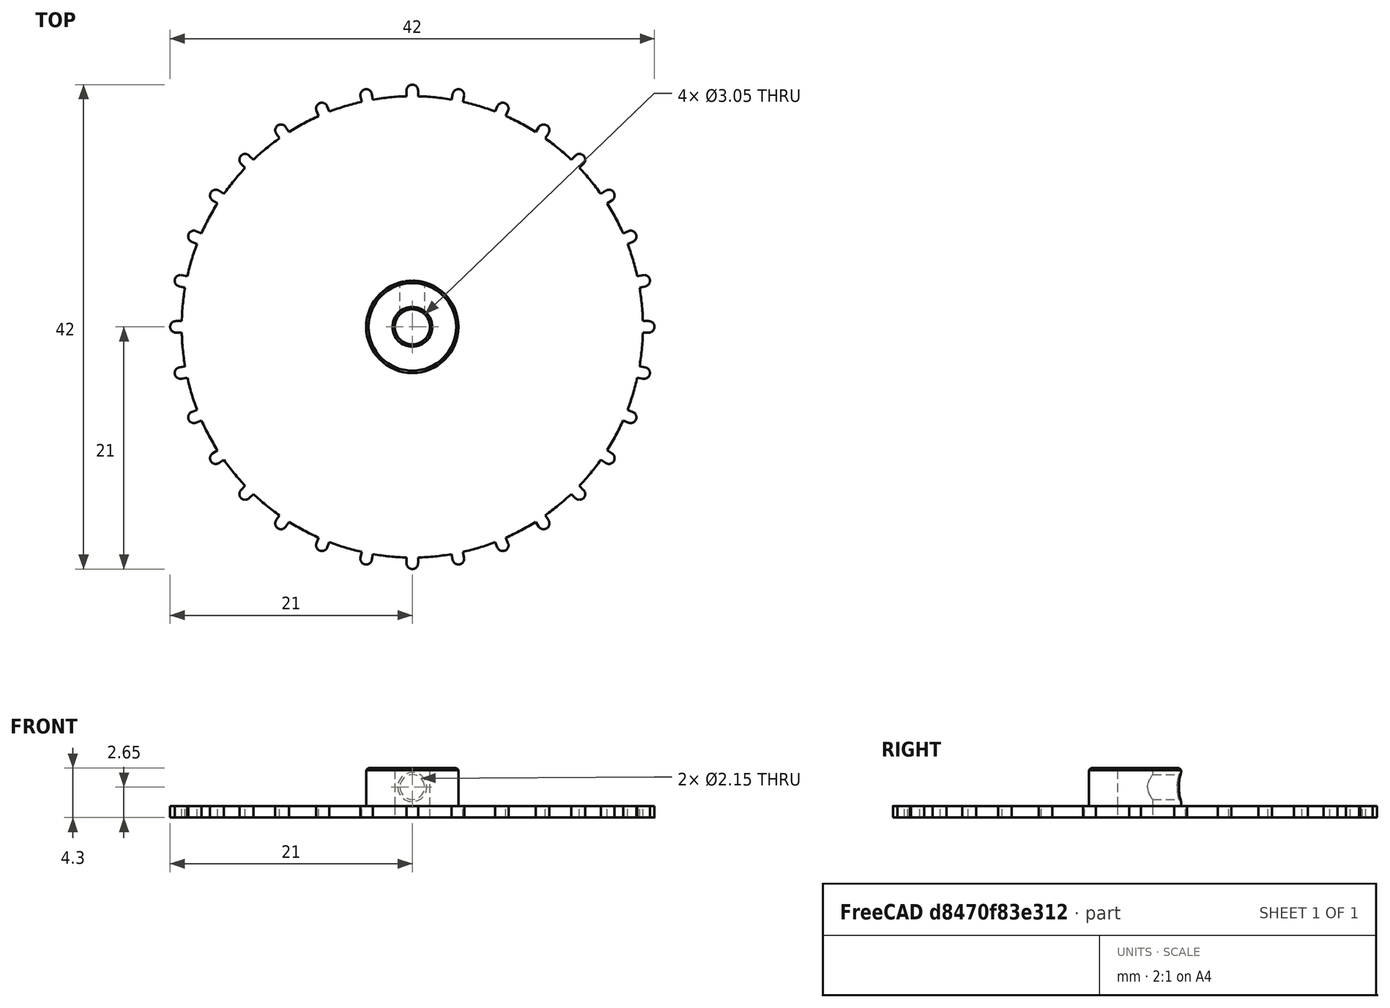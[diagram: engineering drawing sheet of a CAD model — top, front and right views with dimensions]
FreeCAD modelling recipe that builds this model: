
FCSTD DOCUMENT  (FreeCAD 0.20R29603 (Git))
Label: gear-with-hub
License: Other
objects: TechDraw::DrawViewDimension×7, Sketcher::SketchObject×4, PartDesign::Body×3, PartDesign::Pad×2, PartDesign::Chamfer×2, TechDraw::DrawViewPart×2, TechDraw::DrawViewBalloon×2, PartDesign::Hole×1, PartDesign::PolarPattern×1, PartDesign::Pocket×1, PartDesign::Boolean×1, TechDraw::DrawSVGTemplate×1, TechDraw::DrawLeaderLine×1, TechDraw::DrawViewAnnotation×1, TechDraw::DrawPage×1
note: 21 computed .brp shape members not serialized (recipe doc carries the construction recipe); baked Part::Feature solids carry a one-line shape summary decoded from their .brp

FEATURE [Sketcher::SketchObject] Sketch
  FullyConstrained = true
  MapMode = 5
  Support = -> [XY_Plane]
  sketch-geometry (3):
    g0: Circle CenterX=0 CenterY=0 CenterZ=0 NormalX=0 NormalY=0 NormalZ=1 AngleXU=0 Radius=4
    g1: Circle CenterX=0 CenterY=0 CenterZ=0 NormalX=0 NormalY=0 NormalZ=1 AngleXU=0 Radius=1.525
    g2: LineSegment StartX=1.525 StartY=0 StartZ=0 EndX=4 EndY=0 EndZ=0
  constraints (9):
    c: Coincident(g1,g0)
    c: Coincident(g0,g-1)
    c: Diameter(g1) = 3.05
    c: Diameter(g0) = 8
    c: PointOnObject(g2,g1)
    c: PointOnObject(g2,g0)
    c: Horizontal(g2)
    c: PointOnObject(g2,g-1)
    c: DistanceX(g2,g2) = 2.475
FEATURE [PartDesign::Pad] Pad
  Direction = (0,0,1)
  Length = 3.3
  Length2 = 10
  Profile = -> Sketch
  ReferenceAxis = -> Sketch [N_Axis]
  Type = 0
FEATURE [Sketcher::SketchObject] Sketch001
  FullyConstrained = false
  MapMode = 5
  Placement = pos=(0,0,0) rot=(1,0,0;1.5708rad)
  Support = -> [XZ_Plane]
  sketch-geometry (2):
    g0: GeomPoint X=0 Y=1.65 Z=0
    g1: Circle CenterX=0 CenterY=1.65 CenterZ=0 NormalX=0 NormalY=0 NormalZ=1 AngleXU=0 Radius=2.07621
  constraints (3):
    c: PointOnObject(g0,g-2)
    c: Coincident(g1,g0)
    c: DistanceY(g-1,g1) = 1.65
FEATURE [PartDesign::Hole] Hole  label="M2.5x0.45 Hole"
  BaseFeature = -> Pad
  CustomThreadClearance = 0
  Depth = 5
  DepthType = 0
  Diameter = 2.15
  DrillForDepth = false
  DrillPoint = 1
  DrillPointAngle = 118
  HoleCutCountersinkAngle = 90
  HoleCutCustomValues = false
  HoleCutDepth = 0
  HoleCutDiameter = 6.1
  HoleCutType = 0
  ModelThread = false
  Profile = -> Sketch001
  Tapered = false
  TaperedAngle = 90
  ThreadClass = 0
  ThreadDepth = 5
  ThreadDepthType = 0
  ThreadDirection = 0
  ThreadFit = 0
  ThreadSize = 8
  ThreadType = 2
  Threaded = true
  UseCustomThreadClearance = false
FEATURE [PartDesign::Chamfer] Chamfer
  Angle = 45
  Base = -> Hole [Edge4]
  BaseFeature = -> Hole
  ChamferType = 0
  FlipDirection = false
  Size = 0.2
  Size2 = 1
  SupportTransform = false
  UseAllEdges = false
FEATURE [Sketcher::SketchObject] Sketch002
  FullyConstrained = true
  MapMode = 5
  Support = -> [XY_Plane001]
  sketch-geometry (7):
    g0: LineSegment StartX=-0.5 StartY=19.9937 StartZ=0 EndX=-0.5 EndY=20.5 EndZ=0
    g1: ArcOfCircle CenterX=0 CenterY=20.5 CenterZ=0 NormalX=0 NormalY=0 NormalZ=1 AngleXU=0 Radius=0.5 StartAngle=6.28319 EndAngle=9.42478
    g2: LineSegment StartX=0.5 StartY=20.5 StartZ=0 EndX=0.5 EndY=19.9937 EndZ=0
    g3: ArcOfCircle CenterX=0 CenterY=0 CenterZ=0 NormalX=0 NormalY=0 NormalZ=1 AngleXU=0 Radius=20 StartAngle=1.39945 EndAngle=1.54579
    g4: ArcOfCircle CenterX=0 CenterY=0 CenterZ=0 NormalX=0 NormalY=0 NormalZ=1 AngleXU=0 Radius=20 StartAngle=1.54579 EndAngle=1.5958
    g5: LineSegment StartX=-0.5 StartY=19.9937 StartZ=0 EndX=1e-16 EndY=0 EndZ=0
    g6: LineSegment StartX=3.41019 StartY=19.7071 StartZ=0 EndX=0 EndY=0 EndZ=0
  constraints (20):
    c: Coincident(g2,g1)
    c: Vertical(g2)
    c: Coincident(g3,g2)
    c: Diameter(g3) = 40
    c: DistanceY(g3,g1) = 20.5
    c: Coincident(g4,g3)
    c: Coincident(g4,g0)
    c: Coincident(g4,g2)
    c: Tangent(g2,g1)
    c: Coincident(g6,g3)
    c: Coincident(g6,g3)
    c: Angle(g6,g5) = 0.19635
    c: Coincident(g5,g0)
    c: Coincident(g0,g1)
    c: Tangent(g0,g1)
    c: Vertical(g0)
    c: Coincident(g5,g3)
    c: Coincident(g3,g-1)
    c: PointOnObject(g1,g-2)
    c: Diameter(g1) = 1
FEATURE [PartDesign::Pad] Pad001
  Direction = (0,0,1)
  Length = 1
  Length2 = 100
  Profile = -> Sketch002
  Type = 0
FEATURE [Sketcher::SketchObject] Sketch003
  FullyConstrained = true
  MapMode = 5
  Support = -> [XY_Plane001]
  sketch-geometry (22):
    g0: Circle CenterX=0 CenterY=-11 CenterZ=0 NormalX=0 NormalY=0 NormalZ=1 AngleXU=0 Radius=1.5
    g1: Circle CenterX=9.52628 CenterY=5.5 CenterZ=0 NormalX=0 NormalY=0 NormalZ=1 AngleXU=0 Radius=1.5
    g2: Circle CenterX=-9.52628 CenterY=5.5 CenterZ=0 NormalX=0 NormalY=0 NormalZ=1 AngleXU=0 Radius=1.5
    g3: ArcOfCircle CenterX=0 CenterY=10 CenterZ=0 NormalX=0 NormalY=0 NormalZ=1 AngleXU=0 Radius=1.5 StartAngle=3.14159 EndAngle=6.28319
    g4: ArcOfCircle CenterX=-1e-16 CenterY=12 CenterZ=0 NormalX=0 NormalY=0 NormalZ=1 AngleXU=0 Radius=1.5 StartAngle=1e-16 EndAngle=3.14159
    g5: LineSegment StartX=1.5 StartY=10 StartZ=0 EndX=1.5 EndY=12 EndZ=0
    g6: LineSegment StartX=-1.5 StartY=10 StartZ=0 EndX=-1.5 EndY=12 EndZ=0
    g7: ArcOfCircle CenterX=8.66025 CenterY=-5 CenterZ=0 NormalX=0 NormalY=0 NormalZ=1 AngleXU=0 Radius=1.5 StartAngle=1.0472 EndAngle=4.18879
    g8: ArcOfCircle CenterX=10.3923 CenterY=-6 CenterZ=0 NormalX=0 NormalY=0 NormalZ=1 AngleXU=0 Radius=1.5 StartAngle=4.18879 EndAngle=7.33038
    g9: LineSegment StartX=7.91025 StartY=-6.29904 StartZ=0 EndX=9.6423 EndY=-7.29904 EndZ=0
    g10: LineSegment StartX=9.41025 StartY=-3.70096 StartZ=0 EndX=11.1423 EndY=-4.70096 EndZ=0
    g11: ArcOfCircle CenterX=-8.66025 CenterY=-5 CenterZ=0 NormalX=0 NormalY=0 NormalZ=1 AngleXU=0 Radius=1.5 StartAngle=5.23599 EndAngle=8.37758
    g12: ArcOfCircle CenterX=-10.3923 CenterY=-6 CenterZ=0 NormalX=0 NormalY=0 NormalZ=1 AngleXU=0 Radius=1.5 StartAngle=2.0944 EndAngle=5.23599
    g13: LineSegment StartX=-9.41025 StartY=-3.70096 StartZ=0 EndX=-11.1423 EndY=-4.70096 EndZ=0
    g14: LineSegment StartX=-7.91025 StartY=-6.29904 StartZ=0 EndX=-9.6423 EndY=-7.29904 EndZ=0
    g15: LineSegment StartX=-10.3923 StartY=-6 StartZ=0 EndX=-8.66025 EndY=-5 EndZ=0
    g16: LineSegment StartX=8.66025 StartY=-5 StartZ=0 EndX=10.3923 EndY=-6 EndZ=0
    g17: LineSegment StartX=-9.52628 StartY=5.5 StartZ=0 EndX=0 EndY=0 EndZ=0
    g18: LineSegment StartX=9.52628 StartY=5.5 StartZ=0 EndX=0 EndY=0 EndZ=0
    g19: Circle CenterX=0 CenterY=0 CenterZ=0 NormalX=0 NormalY=0 NormalZ=1 AngleXU=0 Radius=1.525
    g20: Circle CenterX=0 CenterY=-4.2625 CenterZ=0 NormalX=0 NormalY=0 NormalZ=1 AngleXU=0 Radius=1.3
    g21: Circle CenterX=0 CenterY=4.2625 CenterZ=0 NormalX=0 NormalY=0 NormalZ=1 AngleXU=0 Radius=1.3
  constraints (55):
    c: PointOnObject(g0,g-2)
    c: Tangent(g3,g6) = 1.5708
    c: Tangent(g3,g5) = -1.5708
    c: Tangent(g5,g4) = -1.5708
    c: Tangent(g6,g4) = 1.5708
    c: Vertical(g5)
    c: Equal(g3,g4)
    c: PointOnObject(g3,g-2)
    c: Tangent(g7,g10) = 1.5708
    c: Tangent(g7,g9) = -1.5708
    c: Tangent(g9,g8) = -1.5708
    c: Tangent(g10,g8) = 1.5708
    c: Equal(g7,g8)
    c: Tangent(g11,g14) = 1.5708
    c: Tangent(g11,g13) = -1.5708
    c: Tangent(g13,g12) = -1.5708
    c: Tangent(g14,g12) = 1.5708
    c: Equal(g11,g12)
    c: Coincident(g15,g12)
    c: Coincident(g15,g11)
    c: Coincident(g16,g7)
    c: Coincident(g16,g8)
    c: Angle(g-1,g16) = 2.61799
    c: Angle(g-1,g15) = 0.523599
    c: Diameter(g11) = 3
    c: Diameter(g7) = 3
    c: Diameter(g3) = 3
    c: PointOnObject(g-1,g15)
    c: PointOnObject(g-1,g16)
    c: Coincident(g17,g2)
    c: Coincident(g17,g-1)
    c: Coincident(g18,g1)
    c: Coincident(g18,g-1)
    c: Angle(g18,g-2) = 1.0472
    c: Angle(g-2,g17) = 1.0472
    c: Distance(g11,g-1) = 10
    c: Distance(g-1,g12) = 12
    c: Distance(g18) = 11
    c: Distance(g17) = 11
    c: Distance(g-1,g0) = 11
    c: Distance(g7,g-1) = 10
    c: Distance(g8,g-1) = 12
    c: Distance(g3,g-1) = 10
    c: Distance(g-1,g4) = 12
    c: Diameter(g1) = 3
    c: Diameter(g2) = 3
    c: Diameter(g0) = 3
    c: Coincident(g19,g-1)
    c: Diameter(g19) = 3.05
    c: PointOnObject(g20,g-2)
    c: Equal(g21,g20)
    c: Symmetric(g21,g20,g-1)
    c: DistanceY(g20,g21) = 8.525
    c: Diameter(g20) = 2.6
    c: Diameter(g19) = 3.05
FEATURE [PartDesign::PolarPattern] PolarPattern
  Angle = 360
  Axis = -> Sketch002 [N_Axis]
  BaseFeature = -> Pad001
  Occurrences = 32
  Originals = -> [Pad001]
FEATURE [PartDesign::Pocket] Pocket
  BaseFeature = -> PolarPattern
  Direction = (0,0,-1)
  Length = 5
  Length2 = 100
  Profile = -> Sketch003
  Reversed = true
  Type = 0
FEATURE [PartDesign::Body] Body001
  Group = -> [Sketch002,Pad001,PolarPattern,Sketch003,Pocket]
  Origin = -> Origin001
  Placement = pos=(0,0,-1) rot=(0,0,1;0rad)
  Tip = -> Pocket
FEATURE [PartDesign::Chamfer] Chamfer001
  Angle = 45
  Base = -> Chamfer [Edge4,Edge8]
  BaseFeature = -> Chamfer
  ChamferType = 0
  FlipDirection = false
  Size = 0.2
  Size2 = 1
  SupportTransform = false
  UseAllEdges = false
FEATURE [PartDesign::Body] Body
  Group = -> [Sketch,Pad,Sketch001,Hole,Chamfer,Chamfer001]
  Origin = -> Origin
  Tip = -> Chamfer001
FEATURE [PartDesign::Boolean] Boolean
  Group = -> [Body001,Body]
  Type = 0
FEATURE [PartDesign::Body] Body002
  Group = -> [Boolean]
  Origin = -> Origin002
  Tip = -> Boolean
FEATURE [TechDraw::DrawSVGTemplate] Template
  EditableTexts = Designed_by_Name=Lucian Chapar; Drawing_number=PENDING; FC-Date=2023-02-15; FC-SC=4:1; FC-SH=1 OF 1; FC-Title=1-piece-gear; Weight=N/A
  Height = 210
  Orientation = 1
  Width = 297
FEATURE [TechDraw::DrawViewPart] View001
  CoarseView = false
  Direction = (-0.366,0.715,0.596)
  Focus = 100
  HardHidden = false
  IsoCount = 0
  IsoHidden = false
  IsoVisible = false
  LockPosition = false
  Perspective = false
  Rotation = 0
  Scale = 4
  ScaleType = 0
  SeamHidden = false
  SeamVisible = false
  SmoothHidden = false
  SmoothVisible = false
  Source = -> [Body002]
  X = 152.816
  XDirection = (-0.887,-0.461,0.009)
  Y = 146.518
FEATURE [TechDraw::DrawViewBalloon] Balloon
  BubbleShape = 1
  EndType = 0
  EndTypeScale = 1
  KinkLength = 21
  LockPosition = false
  OriginX = -2.04745
  OriginY = -0.847764
  Rotation = 0
  Scale = 4
  ScaleType = 0
  ShapeScale = 1
  SourceView = -> View001
  Text = M2.5x0.45 ↧ 7
  TextWrapLen = -1
  X = -24.7749
  Y = -8.90589
FEATURE [TechDraw::DrawLeaderLine] LeaderLine
  AutoHorizontal = true
  EndSymbol = 0
  LeaderParent = -> View001
  LockPosition = true
  Rotation = 0
  Scalable = false
  Scale = 4
  ScaleType = 0
  StartSymbol = 0
  WayPoints = (3) [(0,0,0),(871.108,-115.163,0),(32.482,-115.163,0)]
  X = 1.18375
  Y = 2.07652
FEATURE [TechDraw::DrawViewAnnotation] Annotation001
  Font = osifont
  LineSpace = 80
  LockPosition = false
  MaxWidth = -1
  Rotation = 0
  Scale = 4
  ScaleType = 0
  Text = ⌵0.2x45°
  TextSize = 6
  TextStyle = 0
  X = 257.591
  Y = 163.629
FEATURE [TechDraw::DrawViewDimension] Dimension
  AngleOverride = false
  Arbitrary = true
  ArbitraryTolerances = false
  EqualTolerance = false
  ExtensionAngle = 0
  FormatSpec = ⌀3.05
  FormatSpecOverTolerance = %+.2w
  FormatSpecUnderTolerance = %+.2w
  Inverted = false
  LineAngle = 0
  LockPosition = false
  MeasureType = 1
  OverTolerance = 0
  References2D = -> [View001]
  Rotation = 0
  Scale = 4
  ScaleType = 0
  TheoreticalExact = false
  Type = 5
  UnderTolerance = -0.02
  X = -118.545
  Y = 6.44192
FEATURE [TechDraw::DrawViewDimension] Dimension001
  AngleOverride = false
  Arbitrary = true
  ArbitraryTolerances = false
  EqualTolerance = false
  ExtensionAngle = 0
  FormatSpec = R20
  FormatSpecOverTolerance = %+.2w
  FormatSpecUnderTolerance = %+.2w
  Inverted = false
  LineAngle = 0
  LockPosition = false
  MeasureType = 1
  OverTolerance = 0
  References2D = -> [View001]
  Rotation = 0
  Scale = 4
  ScaleType = 0
  TheoreticalExact = true
  Type = 4
  UnderTolerance = 0
  X = 91.1366
  Y = -42.2632
FEATURE [TechDraw::DrawViewDimension] Dimension002
  AngleOverride = false
  Arbitrary = true
  ArbitraryTolerances = false
  EqualTolerance = true
  ExtensionAngle = 0
  FormatSpec = R0.5
  FormatSpecOverTolerance = %+.2w
  FormatSpecUnderTolerance = %+.2w
  Inverted = false
  LineAngle = 0
  LockPosition = false
  MeasureType = 1
  OverTolerance = 0
  References2D = -> [View001]
  Rotation = 0
  Scale = 4
  ScaleType = 0
  TheoreticalExact = true
  Type = 4
  UnderTolerance = 0
  X = 103.106
  Y = -26.3301
FEATURE [TechDraw::DrawViewPart] View
  CoarseView = false
  Direction = (0,1,0)
  Focus = 100
  HardHidden = false
  IsoCount = 0
  IsoHidden = false
  IsoVisible = false
  LockPosition = true
  Perspective = false
  Rotation = 0
  Scale = 4
  ScaleType = 0
  SeamHidden = false
  SeamVisible = true
  SmoothHidden = false
  SmoothVisible = true
  Source = -> [Body002]
  X = 151.453
  XDirection = (-1,0,0)
  Y = 76.9843
FEATURE [TechDraw::DrawViewDimension] Dimension003
  AngleOverride = false
  Arbitrary = false
  ArbitraryTolerances = false
  EqualTolerance = false
  ExtensionAngle = 0
  FormatSpec = %.2w
  FormatSpecOverTolerance = %+.2w
  FormatSpecUnderTolerance = %+.2w
  Inverted = false
  LineAngle = 0
  LockPosition = false
  MeasureType = 1
  OverTolerance = 0
  References2D = -> [View]
  Rotation = 0
  Scale = 4
  ScaleType = 0
  TheoreticalExact = false
  Type = 2
  UnderTolerance = -0.1
  X = -119.435
  Y = -23.0674
FEATURE [TechDraw::DrawViewDimension] Dimension004
  AngleOverride = false
  Arbitrary = false
  ArbitraryTolerances = false
  EqualTolerance = false
  ExtensionAngle = 0
  FormatSpec = %.2w
  FormatSpecOverTolerance = %+.2w
  FormatSpecUnderTolerance = %+.2w
  Inverted = false
  LineAngle = 0
  LockPosition = false
  MeasureType = 1
  OverTolerance = 0
  References2D = -> [View]
  Rotation = 0
  Scale = 4
  ScaleType = 0
  TheoreticalExact = false
  Type = 2
  UnderTolerance = -0.1
  X = -98.5834
  Y = -23.0567
FEATURE [TechDraw::DrawViewDimension] Dimension005
  AngleOverride = false
  Arbitrary = false
  ArbitraryTolerances = false
  EqualTolerance = false
  ExtensionAngle = 0
  FormatSpec = %.2w
  FormatSpecOverTolerance = %+.2w
  FormatSpecUnderTolerance = %+.2w
  Inverted = false
  LineAngle = 0
  LockPosition = false
  MeasureType = 1
  OverTolerance = 0
  References2D = -> [View]
  Rotation = 0
  Scale = 4
  ScaleType = 0
  TheoreticalExact = true
  Type = 1
  UnderTolerance = 0
  X = 108.894
  Y = -7.59129
FEATURE [TechDraw::DrawViewBalloon] Balloon001
  BubbleShape = 1
  EndType = 0
  EndTypeScale = 1
  KinkLength = 5
  LockPosition = false
  OriginX = 1.20675
  OriginY = 0.666484
  Rotation = 0
  Scale = 4
  ScaleType = 0
  ShapeScale = 1
  SourceView = -> View
  Text = 0.5x45°
  TextWrapLen = -1
  X = 8.66751
  Y = 2.28294
FEATURE [TechDraw::DrawViewDimension] Dimension006
  AngleOverride = false
  Arbitrary = false
  ArbitraryTolerances = false
  EqualTolerance = true
  ExtensionAngle = 0
  FormatSpec = %.2w
  FormatSpecOverTolerance = %+.2w
  FormatSpecUnderTolerance = %+.2w
  Inverted = false
  LineAngle = 0
  LockPosition = false
  MeasureType = 1
  OverTolerance = 0
  References2D = -> [View]
  Rotation = 0
  ScaleType = 2
  TheoreticalExact = false
  Type = 1
  UnderTolerance = 0
  X = -60.3307
  Y = 18.7192
FEATURE [TechDraw::DrawPage] Page
  KeepUpdated = true
  NextBalloonIndex = 4
  ProjectionType = 0
  Scale = 4
  Template = -> Template
  Views = -> [View001,Balloon,LeaderLine,Annotation001,Dimension,Dimension001,Dimension002,View,Dimension003,Dimension004,Dimension005,Balloon001,Dimension006]
